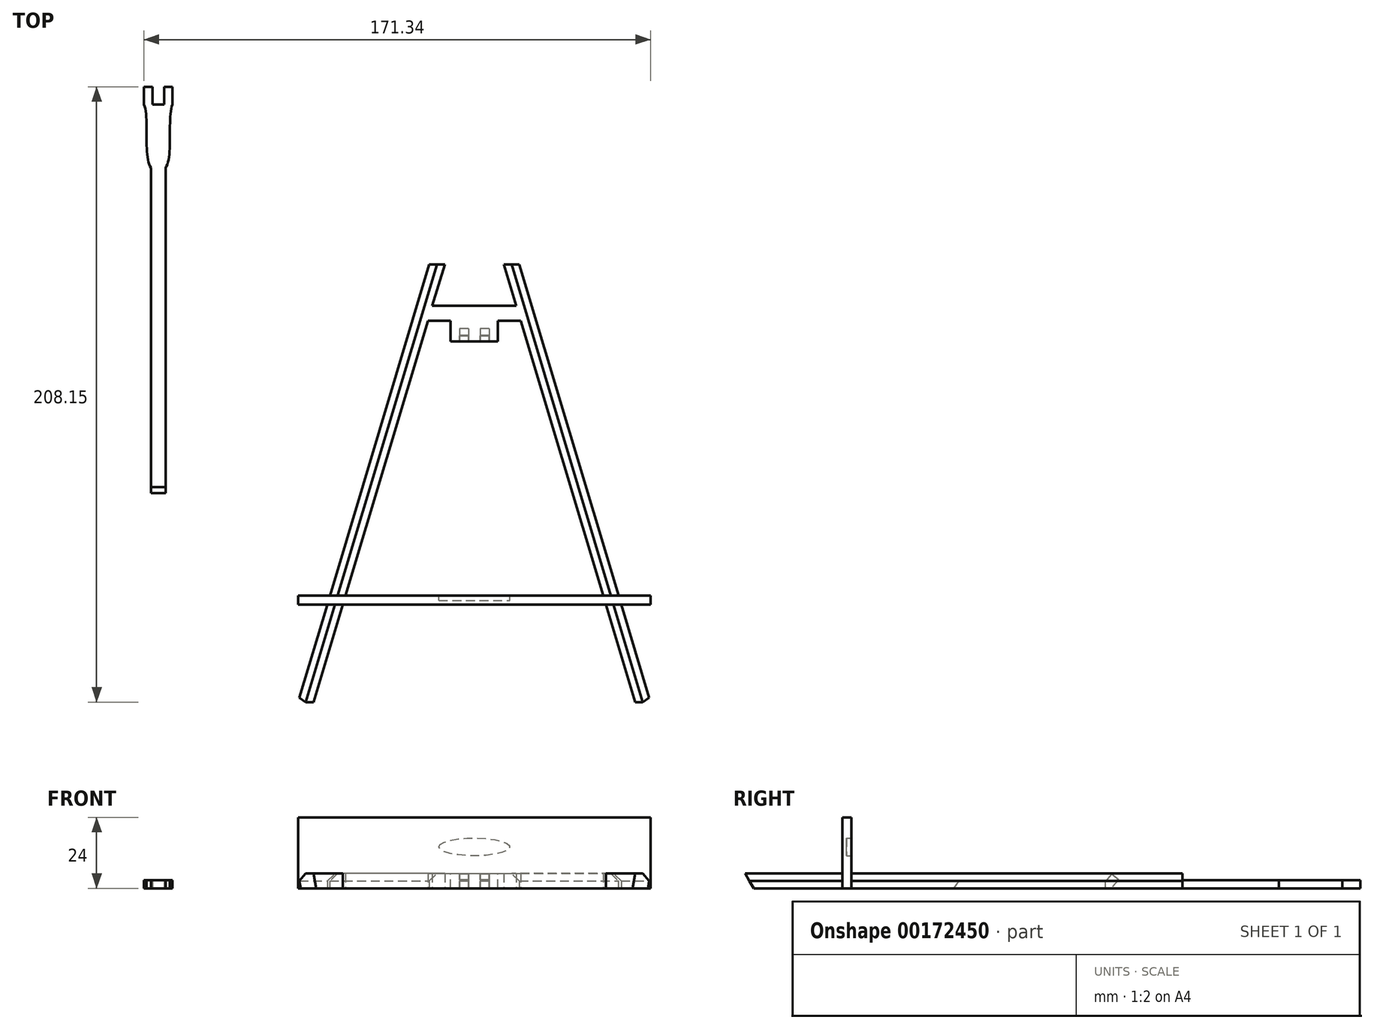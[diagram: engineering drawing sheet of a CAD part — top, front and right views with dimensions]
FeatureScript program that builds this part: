
annotation { "Feature Type Name" : "Feature", "Feature Type Description" : "" }
export const myFeature = defineFeature(function(context is Context, id is Id, definition is map)
    precondition{}
    {
        {
            var Q0;
            Q0=qCreatedBy(makeId("Top.planeOp"),FACE);
            var sketch = newSketch(context, id + "F0", { "sketchPlane" : qUnion([Q0])});
            skLineSegment(sketch, "E0.bottom", {"start": v(-52.21, 78.6) * mm, "end": v(57.79, 78.6) * mm});
            skLineSegment(sketch, "E0.top", {"start": v(-52.21, -71.4) * mm, "end": v(57.79, -71.4) * mm});
            skLineSegment(sketch, "E0.left", {"start": v(-52.21, 78.6) * mm, "end": v(-52.21, -71.4) * mm});
            skLineSegment(sketch, "E0.right", {"start": v(57.79, 78.6) * mm, "end": v(57.79, -71.4) * mm});
            skLineSegment(sketch, "E1", {"start": v(2.79, 78.6) * mm, "end": v(-7.21, 78.6) * mm});
            skLineSegment(sketch, "E2", {"start": v(2.79, 78.6) * mm, "end": v(12.79, 78.6) * mm});
            skLineSegment(sketch, "E3", {"start": v(-7.21, 78.6) * mm, "end": v(-52.21, -71.4) * mm});
            skLineSegment(sketch, "E4", {"start": v(12.79, 78.6) * mm, "end": v(57.79, -71.4) * mm});
            skLineSegment(sketch, "E5", {"start": v(-40.81, -33.4) * mm, "end": v(46.39, -33.4) * mm});
            skLineSegment(sketch, "E6.0", {"start": v(-12, 80.05) * mm, "end": v(-57, -69.95) * mm});
            skLineSegment(sketch, "E7.0", {"start": v(17.58, 80.05) * mm, "end": v(62.58, -69.95) * mm});
            skLineSegment(sketch, "E8.0", {"start": v(-41.71, -36.4) * mm, "end": v(47.29, -36.4) * mm});
            skLineSegment(sketch, "E9", {"start": v(-12, 80.05) * mm, "end": v(-7.21, 78.6) * mm});
            skLineSegment(sketch, "E10", {"start": v(12.79, 78.6) * mm, "end": v(17.58, 80.05) * mm});
            skLineSegment(sketch, "E11", {"start": v(-57, -69.95) * mm, "end": v(-52.21, -71.4) * mm});
            skLineSegment(sketch, "E12", {"start": v(57.79, -71.4) * mm, "end": v(62.58, -69.95) * mm});
            skLineSegment(sketch, "E13", {"start": v(-11.41, 64.6) * mm, "end": v(16.99, 64.6) * mm});
            skLineSegment(sketch, "E14.0", {"start": v(-12.91, 59.6) * mm, "end": v(18.49, 59.6) * mm});
            skLineSegment(sketch, "E15", {"start": v(2.79, 78.6) * mm, "end": v(2.79, 64.6) * mm, "construction": true});
            skLineSegment(sketch, "E16", {"start": v(2.79, -36.4) * mm, "end": v(2.79, -71.4) * mm, "construction": true});
            skSolve(sketch);
        }
        {
            var Q0;
            {var subQ0=sQuery(id+"F0.wireOp",EDGE,"E3");var subQ1=makeQuery(id+"F0.imprint","INTERSECT",VERTEX,{"derivedFrom":[subQ0,sQuery(id+"F0.wireOp",EDGE,"E13")]});Q0=makeQuery(id+"F0.imprint","IMPRINT",FACE,{"disambiguationData":[TD([[makeQuery(id+"F0.imprint","IMPRINT",EDGE,{"disambiguationData":[TD([[subQ1,-1.0]])],"derivedFrom":subQ0}),-1.0]])]});}
            var Q1;
            {var subQ0=sQuery(id+"F0.wireOp",EDGE,"E13");Q1=makeQuery(id+"F0.imprint","IMPRINT",FACE,{"disambiguationData":[TD([[makeQuery(id+"F0.imprint","IMPRINT",EDGE,{"derivedFrom":subQ0}),-1.0]])]});}
            var Q2;
            {var subQ0=sQuery(id+"F0.wireOp",EDGE,"E4");var subQ5=makeQuery(id+"F0.imprint","INTERSECT",VERTEX,{"derivedFrom":[subQ0,sQuery(id+"F0.wireOp",EDGE,"E13")]});Q2=makeQuery(id+"F0.imprint","IMPRINT",FACE,{"disambiguationData":[TD([[makeQuery(id+"F0.imprint","IMPRINT",EDGE,{"disambiguationData":[TD([[subQ5,-1.0]])],"derivedFrom":subQ0}),1.0]])]});}
            var Q3;
            {var subQ0=sQuery(id+"F0.wireOp",EDGE,"E5");Q3=makeQuery(id+"F0.imprint","IMPRINT",FACE,{"disambiguationData":[TD([[makeQuery(id+"F0.imprint","IMPRINT",EDGE,{"derivedFrom":subQ0}),-1.0]])]});}
            var Q4;
            {var subQ0=sQuery(id+"F0.wireOp",EDGE,"E11");Q4=makeQuery(id+"F0.imprint","IMPRINT",FACE,{"disambiguationData":[TD([[makeQuery(id+"F0.imprint","IMPRINT",EDGE,{"derivedFrom":subQ0}),1.0]])]});}
            var Q5;
            {var subQ0=sQuery(id+"F0.wireOp",EDGE,"E12");Q5=makeQuery(id+"F0.imprint","IMPRINT",FACE,{"disambiguationData":[TD([[makeQuery(id+"F0.imprint","IMPRINT",EDGE,{"derivedFrom":subQ0}),1.0]])]});}
            extrude(context, id + "F1", {"entities" : qUnion([Q0, Q1, Q2, Q3, Q4, Q5]), "depth" : 5 * mm});
        }
        {
            var Q0;
            Q0=makeQuery(id+"F1.opExtrude","CAP_FACE",FACE,{"disambiguationData":[OSD([sQuery(id+"F0.wireOp",EDGE,"E0.bottom"),sQuery(id+"F0.wireOp",EDGE,"E3"),sQuery(id+"F0.wireOp",EDGE,"E4"),sQuery(id+"F0.wireOp",EDGE,"E5"),sQuery(id+"F0.wireOp",EDGE,"E6.0"),sQuery(id+"F0.wireOp",EDGE,"E7.0"),sQuery(id+"F0.wireOp",EDGE,"E8.0"),sQuery(id+"F0.wireOp",EDGE,"E11"),sQuery(id+"F0.wireOp",EDGE,"E12"),sQuery(id+"F0.wireOp",EDGE,"E13"),sQuery(id+"F0.wireOp",EDGE,"E14.0")])],"isStart":true});
            var sketch = newSketch(context, id + "F2", { "sketchPlane" : qUnion([Q0])});
            skLineSegment(sketch, "E17.0", {"start": v(-40.81, 33.4) * mm, "end": v(46.39, 33.4) * mm});
            skLineSegment(sketch, "E18.0", {"start": v(-41.71, 36.4) * mm, "end": v(47.29, 36.4) * mm});
            skLineSegment(sketch, "E19", {"start": v(2.79, 3.1) * mm, "end": v(2.79, -57.6) * mm, "construction": true});
            skLineSegment(sketch, "E20", {"start": v(-41.71, 36.4) * mm, "end": v(-56.81, 36.4) * mm});
            skLineSegment(sketch, "E21", {"start": v(-56.81, 33.4) * mm, "end": v(-56.81, 36.4) * mm});
            skLineSegment(sketch, "E22", {"start": v(-56.81, 33.4) * mm, "end": v(-40.81, 33.4) * mm});
            skLineSegment(sketch, "E23.MirrorCS", {"start": v(47.29, 36.4) * mm, "end": v(62.39, 36.4) * mm});
            skLineSegment(sketch, "E24.MirrorCS", {"start": v(62.39, 33.4) * mm, "end": v(62.39, 36.4) * mm});
            skLineSegment(sketch, "E25.MirrorCS", {"start": v(62.39, 33.4) * mm, "end": v(46.39, 33.4) * mm});
            skSolve(sketch);
        }
        {
            var Q0;
            Q0=qSketchRegion(id+"F2",true);
            extrude(context, id + "F3", {"entities" : qUnion([Q0]), "operationType" : NewBodyOperationType.ADD, "oppositeDirection" : true, "depth" : 24 * mm});
        }
        {
            var Q0;
            Q0=makeQuery(id+"F1.opExtrude","SWEPT_FACE",FACE,{"disambiguationData":[OSD([sQuery(id+"F0.wireOp",EDGE,"E14.0")])]});
            var sketch = newSketch(context, id + "F4", { "sketchPlane" : qUnion([Q0])});
            skLineSegment(sketch, "E26.bottom", {"start": v(10.79, 0) * mm, "end": v(-5.21, 0) * mm});
            skLineSegment(sketch, "E26.top", {"start": v(10.79, 5) * mm, "end": v(-5.21, 5) * mm});
            skLineSegment(sketch, "E26.left", {"start": v(10.79, 0) * mm, "end": v(10.79, 5) * mm});
            skLineSegment(sketch, "E26.right", {"start": v(-5.21, 0) * mm, "end": v(-5.21, 5) * mm});
            skLineSegment(sketch, "E27", {"start": v(2.79, 0) * mm, "end": v(2.79, 5) * mm, "construction": true});
            skSolve(sketch);
        }
        {
            var Q0;
            Q0=qSketchRegion(id+"F4",true);
            extrude(context, id + "F5", {"entities" : qUnion([Q0]), "operationType" : NewBodyOperationType.ADD, "depth" : 7 * mm});
        }
        {
            var Q0;
            Q0=makeQuery(id+"F5.opExtrude","CAP_EDGE",EDGE,{"disambiguationData":[OSD([sQuery(id+"F4.wireOp",EDGE,"E26.bottom")])],"isStart":false});
            cPlane(context, id + "F6", {"entities" : qUnion([Q0]), "cplaneType" : CPlaneType.LINE_ANGLE, "offset" : 4 * mm, "angle" : 50 * degree, "width" : 150 * mm, "height" : 150 * mm});
        }
        {
            var Q0;
            Q0=qCreatedBy(id+"F6.planeOp",FACE);
            var sketch = newSketch(context, id + "F7", { "sketchPlane" : qUnion([Q0])});
            skLineSegment(sketch, "E28.bottom", {"start": v(-0.79, -27.8) * mm, "end": v(2.21, -27.8) * mm});
            skLineSegment(sketch, "E28.top", {"start": v(-0.79, -24.8) * mm, "end": v(2.21, -24.8) * mm});
            skLineSegment(sketch, "E28.left", {"start": v(-0.79, -27.8) * mm, "end": v(-0.79, -24.8) * mm});
            skPoint(sketch, "E29.0", {"position": v(10.79, 40.3) * mm});
            skPoint(sketch, "E29.1", {"position": v(-5.21, 40.3) * mm});
            skLineSegment(sketch, "E30.bottom", {"start": v(7.79, 41.8) * mm, "end": v(4.79, 41.8) * mm});
            skLineSegment(sketch, "E30.top", {"start": v(7.79, 38.8) * mm, "end": v(4.79, 38.8) * mm});
            skLineSegment(sketch, "E30.left", {"start": v(7.79, 41.8) * mm, "end": v(7.79, 38.8) * mm});
            skLineSegment(sketch, "E30.right", {"start": v(4.79, 41.8) * mm, "end": v(4.79, 38.8) * mm});
            skLineSegment(sketch, "E31", {"start": v(10.79, 40.3) * mm, "end": v(7.79, 40.3) * mm, "construction": true});
            skLineSegment(sketch, "E32", {"start": v(10.79, 40.3) * mm, "end": v(-5.21, 40.3) * mm, "construction": true});
            skLineSegment(sketch, "E33.bottom", {"start": v(0.79, 41.8) * mm, "end": v(-2.21, 41.8) * mm});
            skLineSegment(sketch, "E33.top", {"start": v(0.79, 38.8) * mm, "end": v(-2.21, 38.8) * mm});
            skLineSegment(sketch, "E33.left", {"start": v(0.79, 41.8) * mm, "end": v(0.79, 38.8) * mm});
            skLineSegment(sketch, "E33.right", {"start": v(-2.21, 41.8) * mm, "end": v(-2.21, 38.8) * mm});
            skLineSegment(sketch, "E34", {"start": v(-5.21, 40.3) * mm, "end": v(-2.21, 40.3) * mm, "construction": true});
            skSolve(sketch);
        }
        {
            var Q0;
            Q0=qSketchRegion(id+"F7",true);
            extrude(context, id + "F8", {"entities" : qUnion([Q0]), "operationType" : NewBodyOperationType.REMOVE, "depth" : 5 * mm});
        }
        {
            var Q0;
            Q0=qCreatedBy(makeId("Top.planeOp"),FACE);
            var sketch = newSketch(context, id + "F9", { "sketchPlane" : qUnion([Q0])});
            skLineSegment(sketch, "E35.bottom", {"start": v(-101.65, 1.29) * mm, "end": v(-106.65, 1.29) * mm});
            skLineSegment(sketch, "E35.top", {"start": v(-101.65, 111.29) * mm, "end": v(-106.65, 111.29) * mm});
            skLineSegment(sketch, "E35.left", {"start": v(-101.65, 1.29) * mm, "end": v(-101.65, 111.29) * mm});
            skLineSegment(sketch, "E35.right", {"start": v(-106.65, 1.29) * mm, "end": v(-106.65, 111.29) * mm});
            skPoint(sketch, "E35.middle", {"position": v(-104.15, 56.29) * mm});
            skLineSegment(sketch, "E36.bottom", {"start": v(-99.35, 138.76) * mm, "end": v(-102.15, 138.76) * mm});
            skLineSegment(sketch, "E36.top", {"start": v(-99.35, 132.76) * mm, "end": v(-102.15, 132.76) * mm});
            skLineSegment(sketch, "E36.left", {"start": v(-99.35, 138.76) * mm, "end": v(-99.35, 132.76) * mm});
            skLineSegment(sketch, "E36.right", {"start": v(-102.15, 138.76) * mm, "end": v(-102.15, 132.76) * mm});
            skLineSegment(sketch, "E37.bottom", {"start": v(-106.15, 138.76) * mm, "end": v(-108.95, 138.76) * mm});
            skLineSegment(sketch, "E37.top", {"start": v(-106.15, 132.76) * mm, "end": v(-108.95, 132.76) * mm});
            skLineSegment(sketch, "E37.left", {"start": v(-106.15, 138.76) * mm, "end": v(-106.15, 132.76) * mm});
            skLineSegment(sketch, "E37.right", {"start": v(-108.95, 138.76) * mm, "end": v(-108.95, 132.76) * mm});
            skLineSegment(sketch, "E38", {"start": v(-101.65, 111.29) * mm, "end": v(-101.65, 132.76) * mm, "construction": true});
            skLineSegment(sketch, "E39", {"start": v(-106.65, 111.29) * mm, "end": v(-106.65, 132.76) * mm, "construction": true});
            skLineSegment(sketch, "E40", {"start": v(-101.65, 132.76) * mm, "end": v(-106.65, 132.76) * mm, "construction": true});
            skLineSegment(sketch, "E41", {"start": v(-102.15, 132.76) * mm, "end": v(-101.65, 132.76) * mm, "construction": true});
            skLineSegment(sketch, "E42", {"start": v(-106.15, 132.76) * mm, "end": v(-106.65, 132.76) * mm, "construction": true});
            skFitSpline(sketch, "E43", {"points": [v(-99.35, 132.76) * mm, v(-101.65, 111.29) * mm, v(-106.65, 111.29) * mm, v(-108.95, 132.76) * mm], "startDerivative": vector(-13.95, -37.86) * mm, "endDerivative": vector(-13.95, 37.86) * mm});
            skLineSegment(sketch, "E44", {"start": v(-102.15, 132.76) * mm, "end": v(-106.15, 132.76) * mm});
            skSolve(sketch);
        }
        {
            var Q0;
            Q0=makeQuery(id+"F9.imprint","IMPRINT",FACE,{"disambiguationData":[TD([[makeQuery(id+"F9.imprint","IMPRINT",EDGE,{"derivedFrom":sQuery(id+"F9.wireOp",EDGE,"E35.bottom")}),-1.0]])]});
            var Q1;
            {var subQ1=sQuery(id+"F9.wireOp",EDGE,"E35.top");Q1=makeQuery(id+"F9.imprint","IMPRINT",FACE,{"disambiguationData":[TD([[makeQuery(id+"F9.imprint","IMPRINT",EDGE,{"derivedFrom":subQ1}),-1.0]])]});}
            var Q2;
            Q2=makeQuery(id+"F9.imprint","IMPRINT",FACE,{"disambiguationData":[TD([[makeQuery(id+"F9.imprint","IMPRINT",EDGE,{"derivedFrom":sQuery(id+"F9.wireOp",EDGE,"E36.bottom")}),1.0]])]});
            var Q3;
            Q3=makeQuery(id+"F9.imprint","IMPRINT",FACE,{"disambiguationData":[TD([[makeQuery(id+"F9.imprint","IMPRINT",EDGE,{"derivedFrom":sQuery(id+"F9.wireOp",EDGE,"E37.bottom")}),1.0]])]});
            var Q4;
            {var subQ0=sQuery(id+"F9.wireOp",EDGE,"E35.top");Q4=makeQuery(id+"F9.imprint","IMPRINT",FACE,{"disambiguationData":[TD([[makeQuery(id+"F9.imprint","IMPRINT",EDGE,{"derivedFrom":subQ0}),1.0]])]});}
            extrude(context, id + "F10", {"entities" : qUnion([Q0, Q1, Q2, Q3, Q4]), "depth" : 2.8 * mm});
        }
        {
            var Q0;
            Q0=makeQuery(id+"F10.opExtrude","CAP_EDGE",EDGE,{"disambiguationData":[OSD([sQuery(id+"F9.wireOp",EDGE,"E35.bottom")])],"isStart":false});
            chamfer(context, id + "F11", {"entities" : qUnion([Q0]), "chamferType" : ChamferType.TWO_OFFSETS, "width1" : 2.8 * mm, "oppositeDirection" : false, "width2" : 2 * mm, "tangentPropagation" : true});
        }
        {
            var Q0;
            Q0=makeQuery(id+"F1.opExtrude","CAP_VERTEX",VERTEX,{"disambiguationData":[OSD([sQuery(id+"F0.wireOp",EDGE,"E0.top"),sQuery(id+"F0.wireOp",EDGE,"E0.left"),sQuery(id+"F0.wireOp",EDGE,"E3"),sQuery(id+"F0.wireOp",EDGE,"E11")])],"isStart":false});
            var Q1;
            Q1=makeQuery(id+"F1.opExtrude","CAP_VERTEX",VERTEX,{"disambiguationData":[OSD([sQuery(id+"F0.wireOp",EDGE,"E0.top"),sQuery(id+"F0.wireOp",EDGE,"E0.right"),sQuery(id+"F0.wireOp",EDGE,"E4"),sQuery(id+"F0.wireOp",EDGE,"E12")])],"isStart":false});
            var Q2;
            Q2=makeQuery(id+"F1.opExtrude","CAP_VERTEX",VERTEX,{"disambiguationData":[OSD([sQuery(id+"F0.wireOp",EDGE,"E0.top"),sQuery(id+"F0.wireOp",EDGE,"E0.right"),sQuery(id+"F0.wireOp",EDGE,"E4"),sQuery(id+"F0.wireOp",EDGE,"E12")])],"isStart":true});
            cPlane(context, id + "F12", {"entities" : qUnion([Q0, Q1, Q2]), "cplaneType" : CPlaneType.THREE_POINT, "offset" : 150 * mm, "width" : 150 * mm, "height" : 150 * mm});
        }
        {
            var Q0;
            Q0=qCreatedBy(id+"F12.planeOp",FACE);
            var sketch = newSketch(context, id + "F13", { "sketchPlane" : qUnion([Q0])});
            skLineSegment(sketch, "E45.bottom", {"start": v(-65.92, 12.39) * mm, "end": v(74.93, 12.39) * mm});
            skLineSegment(sketch, "E45.top", {"start": v(-65.92, -10.23) * mm, "end": v(74.93, -10.23) * mm});
            skLineSegment(sketch, "E45.left", {"start": v(-65.92, 12.39) * mm, "end": v(-65.92, -10.23) * mm});
            skLineSegment(sketch, "E45.right", {"start": v(74.93, 12.39) * mm, "end": v(74.93, -10.23) * mm});
            skSolve(sketch);
        }
        {
            var Q0;
            Q0=qSketchRegion(id+"F13",true);
            extrude(context, id + "F14", {"entities" : qUnion([Q0]), "operationType" : NewBodyOperationType.REMOVE, "oppositeDirection" : true, "depth" : 2 * mm});
        }
        {
            var Q0;
            {var subQ0=sQuery(id+"F0.wireOp",EDGE,"E8.0");var subQ2=sQuery(id+"F0.wireOp",EDGE,"E14.0");var subQ3=sQuery(id+"F0.wireOp",EDGE,"E13");var subQ4=sQuery(id+"F0.wireOp",EDGE,"E12");var subQ5=sQuery(id+"F0.wireOp",EDGE,"E11");var subQ6=sQuery(id+"F0.wireOp",EDGE,"E7.0");var subQ7=sQuery(id+"F0.wireOp",EDGE,"E6.0");var subQ8=sQuery(id+"F0.wireOp",EDGE,"E5");var subQ9=sQuery(id+"F0.wireOp",EDGE,"E4");var subQ10=sQuery(id+"F0.wireOp",EDGE,"E3");var subQ11=sQuery(id+"F0.wireOp",EDGE,"E0.bottom");var subQ14=sQuery(id+"F2.wireOp",EDGE,"E25.MirrorCS");var subQ15=sQuery(id+"F2.wireOp",EDGE,"E22");var subQ16=sQuery(id+"F2.wireOp",EDGE,"E17.0");var subQ18=sQuery(id+"F2.wireOp",EDGE,"E23.MirrorCS");var subQ19=sQuery(id+"F2.wireOp",EDGE,"E20");var subQ20=sQuery(id+"F2.wireOp",EDGE,"E18.0");var subQ22=sQuery(id+"F2.wireOp",EDGE,"E24.MirrorCS");var subQ23=sQuery(id+"F2.wireOp",EDGE,"E21");var subQ24=makeQuery(id+"F3.opExtrude","CAP_FACE",FACE,{"disambiguationData":[OSD([subQ16,subQ20,subQ19,subQ23,subQ15,subQ18,subQ22,subQ14])],"isStart":true});Q0=makeQuery(id+"F14.boolean.opBoolean","INTERSECT",EDGE,{"disambiguationData":[OD(1.0)],"derivedFrom":[makeQuery(id+"FEiG26peZH11kR7_2.boolean.opBoolean","MERGE",FACE,{"derivedFrom":[makeQuery(id+"F5.boolean.opBoolean","MERGE",FACE,{"derivedFrom":[makeQuery(id+"F1.opExtrude","CAP_FACE",FACE,{"disambiguationData":[OSD([subQ11,subQ10,subQ9,subQ8,subQ7,subQ6,subQ0,subQ5,subQ4,subQ3,subQ2])],"isStart":true}),makeQuery(id+"F5.opExtrude","SWEPT_FACE",FACE,{"disambiguationData":[OSD([sQuery(id+"F4.wireOp",EDGE,"E26.bottom")])]})]}),makeQuery(id+"FEiG26peZH11kR7_2.opExtrude","CAP_FACE",FACE,{"disambiguationData":[OSD([subQ16,subQ20,subQ19,subQ23,subQ15,subQ18,subQ22,subQ14]),TDD([makeQuery(id+"F3.boolean.opBoolean","SPLIT",FACE,{"disambiguationData":[TD([makeQuery(id+"F1.opExtrude","SWEPT_FACE",FACE,{"disambiguationData":[OSD([subQ7])]})])],"derivedFrom":subQ24})])],"isStart":false}),makeQuery(id+"FEiG26peZH11kR7_2.opExtrude","CAP_FACE",FACE,{"disambiguationData":[OSD([subQ16,subQ20,subQ19,subQ23,subQ15,subQ18,subQ22,subQ14]),TDD([makeQuery(id+"F3.boolean.opBoolean","SPLIT",FACE,{"disambiguationData":[TD([makeQuery(id+"F1.opExtrude","SWEPT_FACE",FACE,{"disambiguationData":[OSD([subQ6])]})])],"derivedFrom":subQ24})])],"isStart":false})]}),makeQuery(id+"F14.opExtrude","CAP_FACE",FACE,{"disambiguationData":[OSD([sQuery(id+"F13.wireOp",EDGE,"E45.bottom"),sQuery(id+"F13.wireOp",EDGE,"E45.top"),sQuery(id+"F13.wireOp",EDGE,"E45.left"),sQuery(id+"F13.wireOp",EDGE,"E45.right")])],"isStart":false})]});}
            var Q1;
            {var subQ0=sQuery(id+"F0.wireOp",EDGE,"E8.0");var subQ2=sQuery(id+"F0.wireOp",EDGE,"E14.0");var subQ3=sQuery(id+"F0.wireOp",EDGE,"E13");var subQ4=sQuery(id+"F0.wireOp",EDGE,"E12");var subQ5=sQuery(id+"F0.wireOp",EDGE,"E11");var subQ6=sQuery(id+"F0.wireOp",EDGE,"E7.0");var subQ7=sQuery(id+"F0.wireOp",EDGE,"E6.0");var subQ8=sQuery(id+"F0.wireOp",EDGE,"E5");var subQ9=sQuery(id+"F0.wireOp",EDGE,"E4");var subQ10=sQuery(id+"F0.wireOp",EDGE,"E3");var subQ11=sQuery(id+"F0.wireOp",EDGE,"E0.bottom");var subQ14=sQuery(id+"F2.wireOp",EDGE,"E25.MirrorCS");var subQ15=sQuery(id+"F2.wireOp",EDGE,"E22");var subQ16=sQuery(id+"F2.wireOp",EDGE,"E17.0");var subQ18=sQuery(id+"F2.wireOp",EDGE,"E23.MirrorCS");var subQ19=sQuery(id+"F2.wireOp",EDGE,"E20");var subQ20=sQuery(id+"F2.wireOp",EDGE,"E18.0");var subQ22=sQuery(id+"F2.wireOp",EDGE,"E24.MirrorCS");var subQ23=sQuery(id+"F2.wireOp",EDGE,"E21");var subQ24=makeQuery(id+"F3.opExtrude","CAP_FACE",FACE,{"disambiguationData":[OSD([subQ16,subQ20,subQ19,subQ23,subQ15,subQ18,subQ22,subQ14])],"isStart":true});Q1=makeQuery(id+"F14.boolean.opBoolean","INTERSECT",EDGE,{"disambiguationData":[OD(0.0)],"derivedFrom":[makeQuery(id+"FEiG26peZH11kR7_2.boolean.opBoolean","MERGE",FACE,{"derivedFrom":[makeQuery(id+"F5.boolean.opBoolean","MERGE",FACE,{"derivedFrom":[makeQuery(id+"F1.opExtrude","CAP_FACE",FACE,{"disambiguationData":[OSD([subQ11,subQ10,subQ9,subQ8,subQ7,subQ6,subQ0,subQ5,subQ4,subQ3,subQ2])],"isStart":true}),makeQuery(id+"F5.opExtrude","SWEPT_FACE",FACE,{"disambiguationData":[OSD([sQuery(id+"F4.wireOp",EDGE,"E26.bottom")])]})]}),makeQuery(id+"FEiG26peZH11kR7_2.opExtrude","CAP_FACE",FACE,{"disambiguationData":[OSD([subQ16,subQ20,subQ19,subQ23,subQ15,subQ18,subQ22,subQ14]),TDD([makeQuery(id+"F3.boolean.opBoolean","SPLIT",FACE,{"disambiguationData":[TD([makeQuery(id+"F1.opExtrude","SWEPT_FACE",FACE,{"disambiguationData":[OSD([subQ7])]})])],"derivedFrom":subQ24})])],"isStart":false}),makeQuery(id+"FEiG26peZH11kR7_2.opExtrude","CAP_FACE",FACE,{"disambiguationData":[OSD([subQ16,subQ20,subQ19,subQ23,subQ15,subQ18,subQ22,subQ14]),TDD([makeQuery(id+"F3.boolean.opBoolean","SPLIT",FACE,{"disambiguationData":[TD([makeQuery(id+"F1.opExtrude","SWEPT_FACE",FACE,{"disambiguationData":[OSD([subQ6])]})])],"derivedFrom":subQ24})])],"isStart":false})]}),makeQuery(id+"F14.opExtrude","CAP_FACE",FACE,{"disambiguationData":[OSD([sQuery(id+"F13.wireOp",EDGE,"E45.bottom"),sQuery(id+"F13.wireOp",EDGE,"E45.top"),sQuery(id+"F13.wireOp",EDGE,"E45.left"),sQuery(id+"F13.wireOp",EDGE,"E45.right")])],"isStart":false})]});}
            chamfer(context, id + "F15", {"entities" : qUnion([Q0, Q1]), "chamferType" : ChamferType.TWO_OFFSETS, "width1" : 5 * mm, "oppositeDirection" : false, "width2" : 3 * mm, "tangentPropagation" : true});
        }
        {
            var Q0;
            Q0=makeQuery(id+"F3.boolean.opBoolean","MERGE",FACE,{"derivedFrom":[makeQuery(id+"F1.opExtrude","SWEPT_FACE",FACE,{"disambiguationData":[OSD([sQuery(id+"F0.wireOp",EDGE,"E5")])]}),makeQuery(id+"F3.opExtrude","SWEPT_FACE",FACE,{"disambiguationData":[OSD([sQuery(id+"F2.wireOp",EDGE,"E17.0"),sQuery(id+"F2.wireOp",EDGE,"E22"),sQuery(id+"F2.wireOp",EDGE,"E25.MirrorCS")])]})]});
            var sketch = newSketch(context, id + "F16", { "sketchPlane" : qUnion([Q0])});
            skLineSegment(sketch, "E46.0", {"start": v(40.81, 0) * mm, "end": v(-46.39, 0) * mm, "construction": true});
            skLineSegment(sketch, "E47", {"start": v(-2.79, 0) * mm, "end": v(-2.79, 14) * mm, "construction": true});
            skEllipse(sketch, "E48", {"center": v(-2.79, 14) * mm, "majorRadius": 12 * mm, "minorRadius": 3 * mm, "majorAxis": v(1, 0)});
            skSolve(sketch);
        }
        {
            var Q0;
            Q0=makeQuery(id+"F16.imprint","IMPRINT",FACE,{"disambiguationData":[TD([[makeQuery(id+"F16.imprint","IMPRINT",EDGE,{"derivedFrom":sQuery(id+"F16.wireOp",EDGE,"E48")}),1.0]])]});
            extrude(context, id + "F17", {"entities" : qUnion([Q0]), "operationType" : NewBodyOperationType.REMOVE, "oppositeDirection" : true, "depth" : 1.6 * mm});
        }
        {
            var Q0;
            {var subQ0=sQuery(id+"F0.wireOp",EDGE,"E6.0");var subQ1=sQuery(id+"F0.wireOp",EDGE,"E5");Q0=makeQuery(id+"F3.boolean.opBoolean","SPLIT",EDGE,{"disambiguationData":[TD([makeQuery(id+"F1.opExtrude","SWEPT_FACE",FACE,{"disambiguationData":[OSD([subQ1])]})])],"derivedFrom":makeQuery(id+"F1.opExtrude","CAP_EDGE",EDGE,{"disambiguationData":[OSD([subQ0])],"isStart":false})});}
            var Q1;
            {var subQ0=sQuery(id+"F0.wireOp",EDGE,"E7.0");var subQ1=sQuery(id+"F0.wireOp",EDGE,"E5");Q1=makeQuery(id+"F3.boolean.opBoolean","SPLIT",EDGE,{"disambiguationData":[TD([makeQuery(id+"F1.opExtrude","SWEPT_FACE",FACE,{"disambiguationData":[OSD([subQ1])]})])],"derivedFrom":makeQuery(id+"F1.opExtrude","CAP_EDGE",EDGE,{"disambiguationData":[OSD([subQ0])],"isStart":false})});}
            var Q2;
            {var subQ1=sQuery(id+"F0.wireOp",EDGE,"E8.0");var subQ2=sQuery(id+"F0.wireOp",EDGE,"E6.0");Q2=makeQuery(id+"F3.boolean.opBoolean","SPLIT",EDGE,{"disambiguationData":[TD([makeQuery(id+"F1.opExtrude","SWEPT_FACE",FACE,{"disambiguationData":[OSD([subQ1])]})])],"derivedFrom":makeQuery(id+"F1.opExtrude","CAP_EDGE",EDGE,{"disambiguationData":[OSD([subQ2])],"isStart":false})});}
            var Q3;
            {var subQ1=sQuery(id+"F0.wireOp",EDGE,"E8.0");var subQ2=sQuery(id+"F0.wireOp",EDGE,"E7.0");Q3=makeQuery(id+"F3.boolean.opBoolean","SPLIT",EDGE,{"disambiguationData":[TD([makeQuery(id+"F1.opExtrude","SWEPT_FACE",FACE,{"disambiguationData":[OSD([subQ1])]})])],"derivedFrom":makeQuery(id+"F1.opExtrude","CAP_EDGE",EDGE,{"disambiguationData":[OSD([subQ2])],"isStart":false})});}
            chamfer(context, id + "F18", {"entities" : qUnion([Q0, Q1, Q2, Q3]), "width" : 2.5 * mm, "tangentPropagation" : true});
        }
    });
